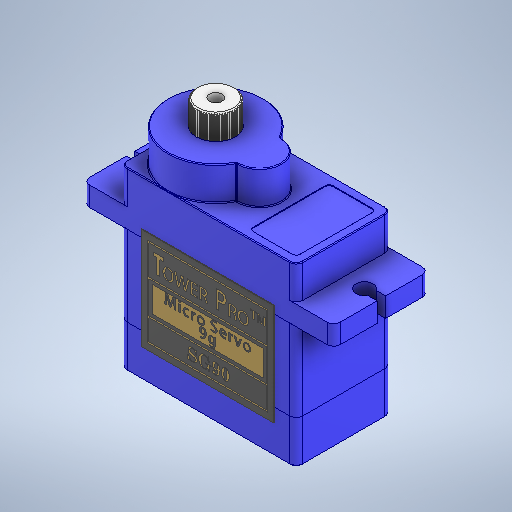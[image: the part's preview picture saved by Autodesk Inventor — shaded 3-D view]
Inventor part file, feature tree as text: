
AUTODESK INVENTOR PART (.ipt)
format: ipt  version: 2025.1 (Build 291241020, 241B)  size: 1,551,360 bytes
history: native  units: in
note: dims shown in document units (in); Inventor stores cm internally (conversion verified against a paired STEP export)
features: other x13, sketch x1
ambient origin geometry x8: Origin, YZ Plane, XZ Plane, XY Plane, X Axis, Y Axis, Z Axis, Center Point
bodies: Solid1 (feature_tree), Solid2 (feature_tree), Solid3 (feature_tree), Solid4 (feature_tree), Solid5 (feature_tree), Solid6 (feature_tree), Solid7 (feature_tree), Solid8 (feature_tree), Solid9 (feature_tree), Solid10 (feature_tree), Solid11 (feature_tree), Solid12 (feature_tree), Solid13 (feature_tree)
feature tree (14):
  sketch  "Sketch1"
  other  "Ressalto-extrusão1"
  other  "Envolver9"
  other  "Corpo-Mover_Copiar1"
  other  "Filete3"
  other  "Espelhar3"
  other  "Espelhar4[1]"
  other  "Espelhar4[2]"
  other  "Corte-extrusão9"
  other  "Ressalto-extrusão13[1]"
  other  "Ressalto-extrusão13[2]"
  other  "Ressalto-extrusão13[3]"
  other  "Furo roscado de M2x0.41[1]"
  other  "PadrãoCircular1"
